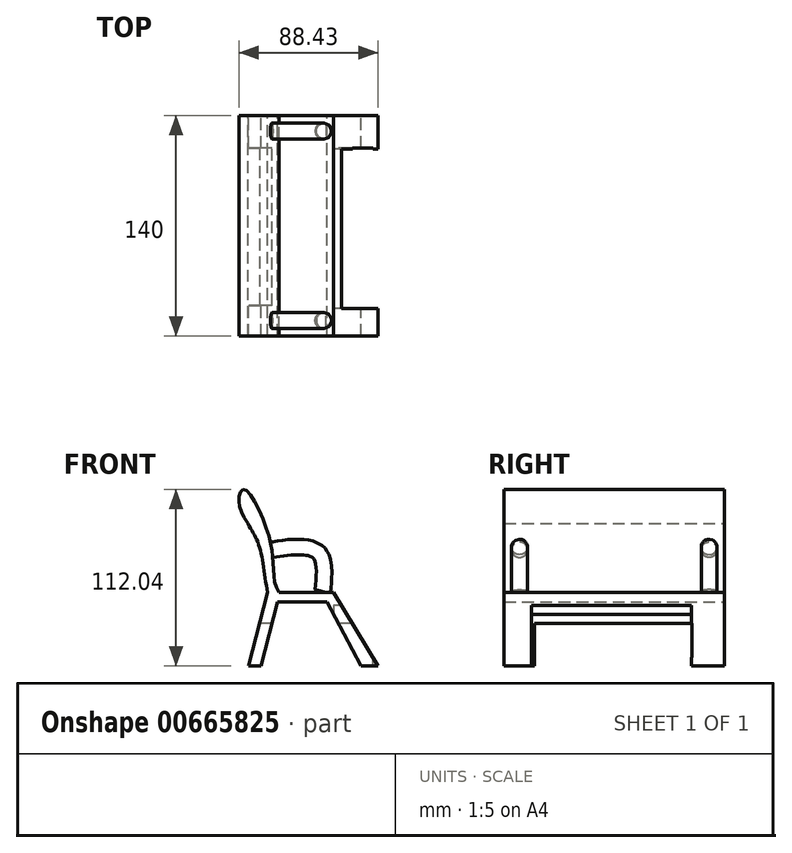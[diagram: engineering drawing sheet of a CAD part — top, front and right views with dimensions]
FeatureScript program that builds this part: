
annotation { "Feature Type Name" : "Feature", "Feature Type Description" : "" }
export const myFeature = defineFeature(function(context is Context, id is Id, definition is map)
    precondition{}
    {
        {
            var Q0;
            Q0=qCreatedBy(makeId("Front.planeOp"),FACE);
            var sketch = newSketch(context, id + "F0", { "sketchPlane" : qUnion([Q0])});
            skFitSpline(sketch, "E0", {"points": [v(-54.45, 43.75) * mm, v(-60.13, 59.27) * mm, v(-56.84, 65.45) * mm, v(-42.45, 40.08) * mm, v(-38.3, 17) * mm, v(-34.62, 0) * mm], "startDerivative": vector(-58.48, 98.34) * mm, "endDerivative": vector(51.28, -65.11) * mm});
            skFitSpline(sketch, "E1", {"points": [v(-54.45, 43.75) * mm, v(-47.05, 28.82) * mm, v(-41.86, 0) * mm], "startDerivative": vector(20, -34.43) * mm, "endDerivative": vector(11.62, -51.73) * mm});
            skLineSegment(sketch, "E2", {"start": v(-41.86, 0) * mm, "end": v(-34.62, 0) * mm});
            skLineSegment(sketch, "E3", {"start": v(-41.86, 0) * mm, "end": v(-54.01, -46.58) * mm});
            skLineSegment(sketch, "E4", {"start": v(-54.01, -46.58) * mm, "end": v(-46.18, -46.58) * mm});
            skLineSegment(sketch, "E5", {"start": v(-46.18, -46.58) * mm, "end": v(-35.75, -6.01) * mm});
            skLineSegment(sketch, "E6", {"start": v(-35.75, -6.01) * mm, "end": v(-4.09, -6.01) * mm});
            skLineSegment(sketch, "E7", {"start": v(-4.09, -6.01) * mm, "end": v(17.37, -46.58) * mm});
            skLineSegment(sketch, "E8", {"start": v(17.37, -46.58) * mm, "end": v(28.27, -46.58) * mm});
            skLineSegment(sketch, "E9", {"start": v(28.27, -46.58) * mm, "end": v(0, 0) * mm});
            skLineSegment(sketch, "E10", {"start": v(0, 0) * mm, "end": v(-34.62, 0) * mm});
            skSolve(sketch);
        }
        {
            var Q0;
            Q0 = qSketchRegion(id + "F0", true);
            extrude(context, id + "F1", {"entities" : qUnion([Q0]), "depth" : 70 * mm, "offsetDistance" : 25 * mm});
        }
        {
            var Q0;
            Q0=qCreatedBy(makeId("Front.planeOp"),FACE);
            cPlane(context, id + "F2", {"entities" : qUnion([Q0]), "cplaneType" : CPlaneType.OFFSET, "offset" : 60 * mm, "width" : 150 * mm, "height" : 150 * mm});
        }
        {
            var Q0;
            Q0=qCreatedBy(id+"F2.planeOp",FACE);
            var sketch = newSketch(context, id + "F3", { "sketchPlane" : qUnion([Q0])});
            skFitSpline(sketch, "E11", {"points": [v(-41.26, 26.23) * mm, v(-21.36, 28.3) * mm, v(-9, 23.49) * mm, v(-7.63, 0) * mm], "startDerivative": vector(59.14, 9.81) * mm, "endDerivative": vector(-7.5, -74.92) * mm});
            skSolve(sketch);
        }
        {
            var Q0;
            Q0=qCreatedBy(makeId("Right.planeOp"),FACE);
            cPlane(context, id + "F4", {"entities" : qUnion([Q0]), "cplaneType" : CPlaneType.OFFSET, "offset" : 42 * mm, "oppositeDirection" : true, "width" : 150 * mm, "height" : 150 * mm});
        }
        {
            var Q0;
            Q0=qCreatedBy(id+"F4.planeOp",FACE);
            var sketch = newSketch(context, id + "F5", { "sketchPlane" : qUnion([Q0])});
            skCircle(sketch, "E12", {"center": v(-60.22, 26.76) * mm, "radius": 5 * mm});
            skSolve(sketch);
        }
        {
            var Q0;
            Q0 = qSketchRegion(id + "F5", true);
            var Q1;
            Q1 = qConstructionFilter(qBodyType(qCreatedBy(id + "F3" ,EDGE), BodyType.WIRE), ConstructionObject.NO);
            sweep(context, id + "F6", {"operationType" : NewBodyOperationType.ADD, "profiles" : qUnion([Q0]), "path" : qUnion([Q1])});
        }
        {
            var Q0;
            Q0=makeQuery(id+"F1.opExtrude","SWEPT_BODY",BODY,{"disambiguationData":[OSD([sQuery(id+"F0.wireOp",EDGE,"E0"),sQuery(id+"F0.wireOp",EDGE,"E1"),sQuery(id+"F0.wireOp",EDGE,"E3"),sQuery(id+"F0.wireOp",EDGE,"E4"),sQuery(id+"F0.wireOp",EDGE,"E5"),sQuery(id+"F0.wireOp",EDGE,"E6"),sQuery(id+"F0.wireOp",EDGE,"E7"),sQuery(id+"F0.wireOp",EDGE,"E8"),sQuery(id+"F0.wireOp",EDGE,"E9"),sQuery(id+"F0.wireOp",EDGE,"E10")])]});
            var Q1;
            Q1=makeQuery(id+"F1.opExtrude","CAP_FACE",FACE,{"disambiguationData":[OSD([sQuery(id+"F0.wireOp",EDGE,"E0"),sQuery(id+"F0.wireOp",EDGE,"E1"),sQuery(id+"F0.wireOp",EDGE,"E3"),sQuery(id+"F0.wireOp",EDGE,"E4"),sQuery(id+"F0.wireOp",EDGE,"E5"),sQuery(id+"F0.wireOp",EDGE,"E6"),sQuery(id+"F0.wireOp",EDGE,"E7"),sQuery(id+"F0.wireOp",EDGE,"E8"),sQuery(id+"F0.wireOp",EDGE,"E9"),sQuery(id+"F0.wireOp",EDGE,"E10")])],"isStart":true});
            mirror(context, id + "F7", {"operationType" : NewBodyOperationType.ADD, "entities" : qUnion([Q0]), "mirrorPlane" : qUnion([Q1])});
        }
        {
            var Q0;
            Q0=qCreatedBy(makeId("Right.planeOp"),FACE);
            var sketch = newSketch(context, id + "F8", { "sketchPlane" : qUnion([Q0])});
            skLineSegment(sketch, "E13.bottom", {"start": v(-50.63, -19.72) * mm, "end": v(49.37, -19.72) * mm});
            skLineSegment(sketch, "E13.top", {"start": v(-50.63, -55.72) * mm, "end": v(49.37, -55.72) * mm});
            skLineSegment(sketch, "E13.left", {"start": v(-50.63, -19.72) * mm, "end": v(-50.63, -55.72) * mm});
            skLineSegment(sketch, "E13.right", {"start": v(49.37, -19.72) * mm, "end": v(49.37, -55.72) * mm});
            skSolve(sketch);
        }
        {
            var Q0;
            Q0=makeQuery(id+"F8.imprint","IMPRINT",FACE,{"disambiguationData":[TD([[makeQuery(id+"F8.imprint","IMPRINT",EDGE,{"derivedFrom":sQuery(id+"F8.wireOp",EDGE,"E13.bottom")}),-1.0]])]});
            extrude(context, id + "F9", {"entities" : qUnion([Q0]), "operationType" : NewBodyOperationType.REMOVE, "depth" : 25 * mm, "offsetDistance" : 25 * mm, "hasSecondDirection" : true, "secondDirectionOppositeDirection" : true, "secondDirectionDepth" : 82 * mm});
        }
        {
            var Q0;
            Q0=qCreatedBy(makeId("Right.planeOp"),FACE);
            var sketch = newSketch(context, id + "F10", { "sketchPlane" : qUnion([Q0])});
            skLineSegment(sketch, "E14.bottom", {"start": v(-52.67, -8.24) * mm, "end": v(48.9, -8.24) * mm});
            skLineSegment(sketch, "E14.top", {"start": v(-52.67, -63.14) * mm, "end": v(48.9, -63.14) * mm});
            skLineSegment(sketch, "E14.left", {"start": v(-52.67, -8.24) * mm, "end": v(-52.67, -63.14) * mm});
            skLineSegment(sketch, "E14.right", {"start": v(48.9, -8.24) * mm, "end": v(48.9, -63.14) * mm});
            skSolve(sketch);
        }
        {
            var Q0;
            Q0=makeQuery(id+"F10.imprint","IMPRINT",FACE,{"disambiguationData":[TD([[makeQuery(id+"F10.imprint","IMPRINT",EDGE,{"derivedFrom":sQuery(id+"F10.wireOp",EDGE,"E14.bottom")}),-1.0]])]});
            extrude(context, id + "F11", {"entities" : qUnion([Q0]), "operationType" : NewBodyOperationType.REMOVE, "depth" : 74 * mm, "offsetDistance" : 25 * mm});
        }
    });
